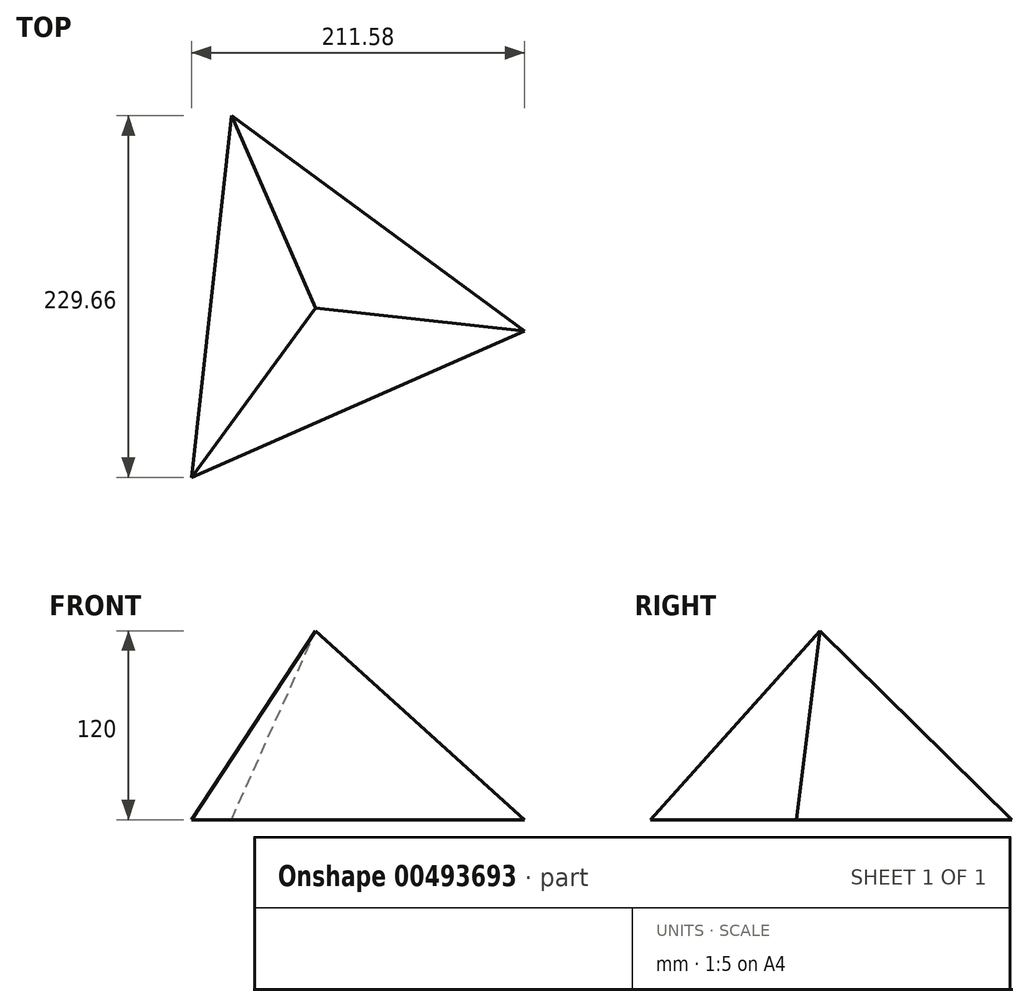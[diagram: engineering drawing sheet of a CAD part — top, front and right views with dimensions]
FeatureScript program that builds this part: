
annotation { "Feature Type Name" : "Feature", "Feature Type Description" : "" }
export const myFeature = defineFeature(function(context is Context, id is Id, definition is map)
    precondition{}
    {
        {
            var Q0;
            Q0=qCreatedBy(makeId("Top.planeOp"),FACE);
            var sketch = newSketch(context, id + "F0", { "sketchPlane" : qUnion([Q0])});
            skCircle(sketch, "E0.cCircle", {"center": v(0, 0) * mm, "radius": 133.4 * mm, "construction": true});
            skLineSegment(sketch, "E0.0", {"start": v(-53.6, 122.16) * mm, "end": v(132.6, -14.66) * mm});
            skLineSegment(sketch, "E0.1", {"start": v(132.6, -14.66) * mm, "end": v(-79, -107.5) * mm});
            skLineSegment(sketch, "E0.2", {"start": v(-79, -107.5) * mm, "end": v(-53.6, 122.16) * mm});
            skSolve(sketch);
        }
        {
            var Q0;
            Q0=qCreatedBy(makeId("Top.planeOp"),FACE);
            cPlane(context, id + "F1", {"entities" : qUnion([Q0]), "cplaneType" : CPlaneType.OFFSET, "offset" : 120 * mm, "width" : 150 * mm, "height" : 150 * mm});
        }
        {
            var Q0;
            Q0=qCreatedBy(id+"F1.planeOp",FACE);
            var sketch = newSketch(context, id + "F2", { "sketchPlane" : qUnion([Q0])});
            skPoint(sketch, "E1", {"position": v(0, 0) * mm});
            skSolve(sketch);
        }
        {
            var Q0;
            Q0=makeQuery(id+"F0.imprint","IMPRINT",FACE,{"disambiguationData":[TD([[makeQuery(id+"F0.imprint","IMPRINT",EDGE,{"derivedFrom":sQuery(id+"F0.wireOp",EDGE,"E0.0")}),-1.0]])]});
            var Q1;
            Q1=sQuery(id+"F2.wireOp",VERTEX,"E1");
            loft(context, id + "F3", {"sheetProfilesArray" : [{ "sheetProfileEntities" : qUnion([Q0]) }, { "sheetProfileEntities" : qUnion([Q1]) }]});
        }
    });
